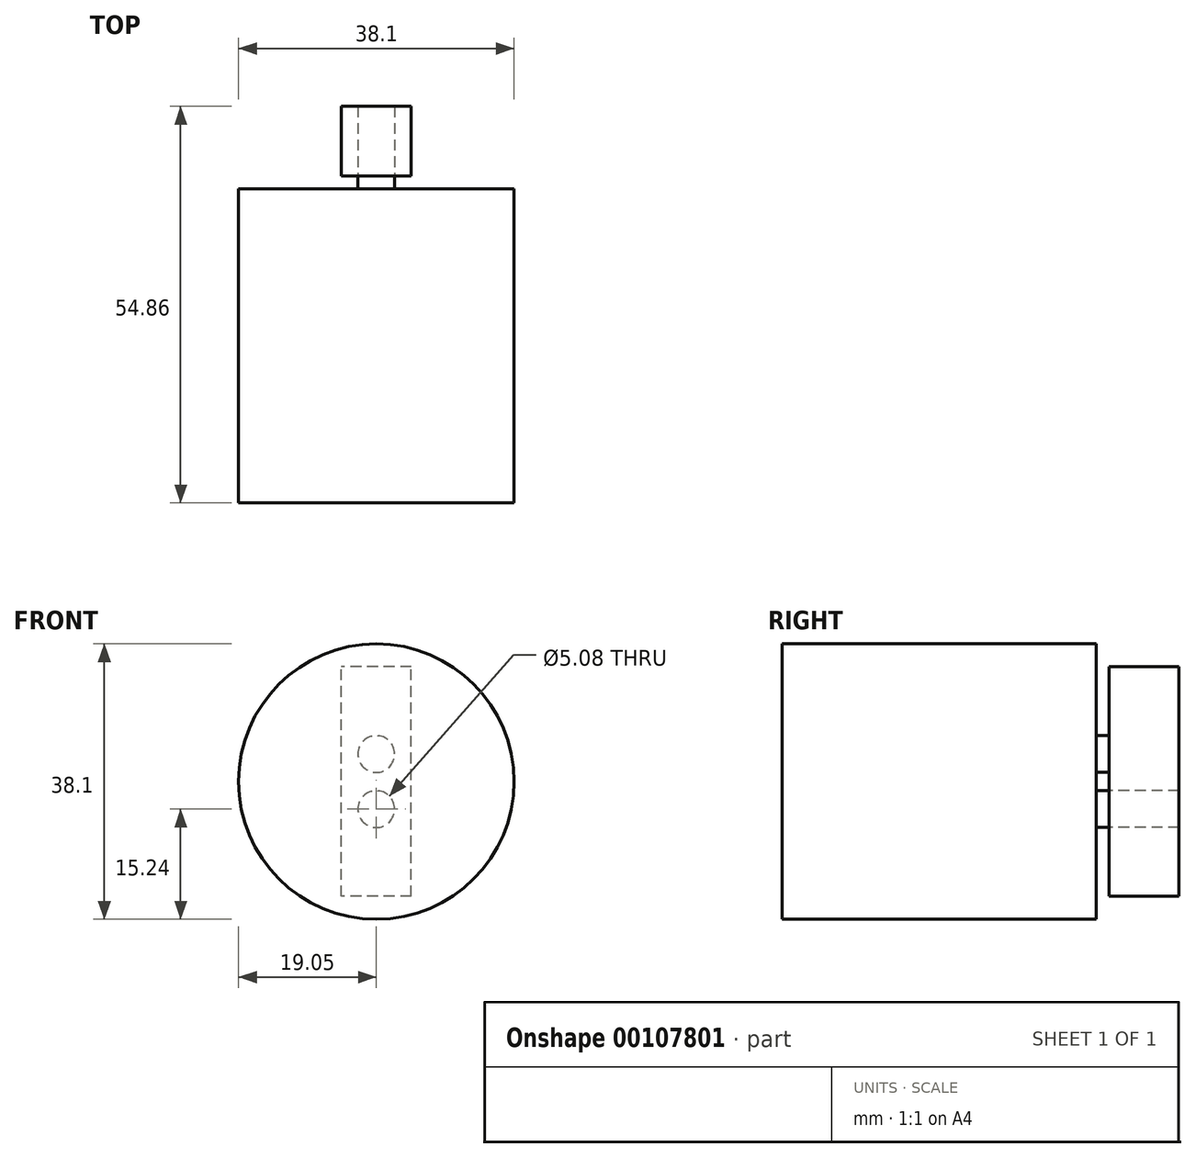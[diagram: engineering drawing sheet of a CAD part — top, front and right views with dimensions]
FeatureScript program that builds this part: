
annotation { "Feature Type Name" : "Feature", "Feature Type Description" : "" }
export const myFeature = defineFeature(function(context is Context, id is Id, definition is map)
    precondition{}
    {
        {
            var Q0;
            Q0=qCreatedBy(makeId("Front.planeOp"),FACE);
            var sketch = newSketch(context, id + "F0", { "sketchPlane" : qUnion([Q0])});
            skCircle(sketch, "E0", {"center": v(0, 0) * mm, "radius": 19.05 * mm});
            skSolve(sketch);
        }
        {
            var Q0;
            Q0=makeQuery(id+"F0.imprint","IMPRINT",FACE,{"disambiguationData":[TD([[makeQuery(id+"F0.imprint","IMPRINT",EDGE,{"derivedFrom":sQuery(id+"F0.wireOp",EDGE,"E0")}),1.0]])]});
            extrude(context, id + "F1", {"entities" : qUnion([Q0]), "depth" : 43.43 * mm});
        }
        {
            var Q0;
            Q0=qCreatedBy(makeId("Front.planeOp"),FACE);
            var sketch = newSketch(context, id + "F2", { "sketchPlane" : qUnion([Q0])});
            skLineSegment(sketch, "E1.bottom", {"start": v(0, -3.81) * mm, "end": v(0, -3.81) * mm});
            skLineSegment(sketch, "E1.top", {"start": v(0, 3.81) * mm, "end": v(0, 3.81) * mm});
            skPoint(sketch, "E1.middle", {"position": v(0, 0) * mm});
            skCircle(sketch, "E2", {"center": v(0, -3.81) * mm, "radius": 2.54 * mm});
            skCircle(sketch, "E3", {"center": v(0, 3.81) * mm, "radius": 2.54 * mm});
            skSolve(sketch);
        }
        {
            var Q0;
            Q0=makeQuery(id+"F2.imprint","IMPRINT",FACE,{"disambiguationData":[TD([[makeQuery(id+"F2.imprint","IMPRINT",EDGE,{"derivedFrom":sQuery(id+"F2.wireOp",EDGE,"E2")}),1.0]])]});
            var Q1;
            Q1=makeQuery(id+"F2.imprint","IMPRINT",FACE,{"disambiguationData":[TD([[makeQuery(id+"F2.imprint","IMPRINT",EDGE,{"derivedFrom":sQuery(id+"F2.wireOp",EDGE,"E3")}),1.0]])]});
            extrude(context, id + "F3", {"entities" : qUnion([Q0, Q1]), "operationType" : NewBodyOperationType.ADD, "oppositeDirection" : true, "depth" : 1.78 * mm});
        }
        {
            var Q0;
            Q0=makeQuery(id+"F3.opExtrude","CAP_FACE",FACE,{"disambiguationData":[OSD([sQuery(id+"F2.wireOp",EDGE,"E2")])],"isStart":false});
            var sketch = newSketch(context, id + "F4", { "sketchPlane" : qUnion([Q0])});
            skLineSegment(sketch, "E4.bottom", {"start": v(-4.83, -15.88) * mm, "end": v(4.83, -15.88) * mm});
            skLineSegment(sketch, "E4.top", {"start": v(-4.83, 15.88) * mm, "end": v(4.83, 15.88) * mm});
            skLineSegment(sketch, "E4.left", {"start": v(-4.83, -15.88) * mm, "end": v(-4.83, 15.88) * mm});
            skLineSegment(sketch, "E4.right", {"start": v(4.83, -15.88) * mm, "end": v(4.83, 15.88) * mm});
            skPoint(sketch, "E4.middle", {"position": v(0, 0) * mm});
            skSolve(sketch);
        }
        {
            var Q0;
            Q0=makeQuery(id+"F4.imprint","IMPRINT",FACE,{"disambiguationData":[TD([[makeQuery(id+"F4.imprint","IMPRINT",EDGE,{"derivedFrom":sQuery(id+"F4.wireOp",EDGE,"E4.bottom")}),1.0]])]});
            extrude(context, id + "F5", {"entities" : qUnion([Q0]), "depth" : 9.65 * mm});
        }
    });
